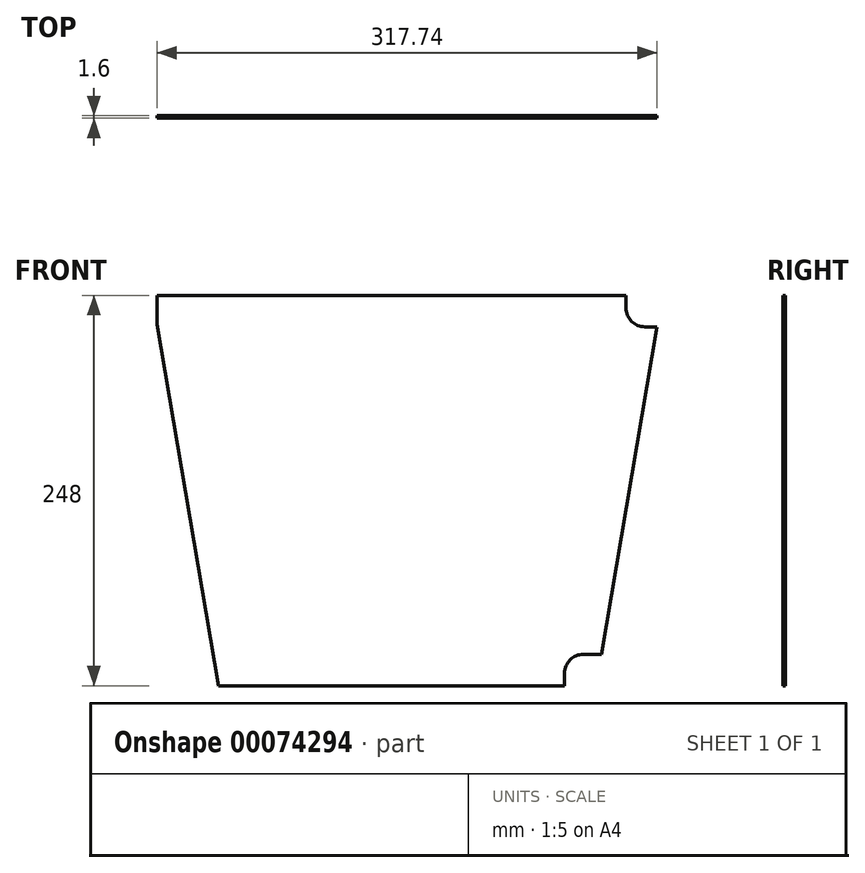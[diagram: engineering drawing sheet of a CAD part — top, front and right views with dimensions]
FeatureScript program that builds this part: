
annotation { "Feature Type Name" : "Feature", "Feature Type Description" : "" }
export const myFeature = defineFeature(function(context is Context, id is Id, definition is map)
    precondition{}
    {
        {
            var Q0;
            Q0=qCreatedBy(makeId("Front.planeOp"),FACE);
            var sketch = newSketch(context, id + "F0", { "sketchPlane" : qUnion([Q0])});
            skLineSegment(sketch, "E0.bottom", {"start": v(-165, 30.18) * mm, "end": v(165, 30.18) * mm});
            skLineSegment(sketch, "E0.left", {"start": v(-165, 30.18) * mm, "end": v(-165, 5.18) * mm});
            skLineSegment(sketch, "E0.right", {"start": v(165, 30.18) * mm, "end": v(165, 5.18) * mm});
            skLineSegment(sketch, "E1.top", {"start": v(-125, -229.82) * mm, "end": v(125, -229.82) * mm});
            skLineSegment(sketch, "E2", {"start": v(0, 0) * mm, "end": v(0, -253.16) * mm, "construction": true});
            skLineSegment(sketch, "E3", {"start": v(-165, 5.18) * mm, "end": v(-125, -229.82) * mm});
            skLineSegment(sketch, "E4", {"start": v(165, 5.18) * mm, "end": v(125, -229.82) * mm});
            skPoint(sketch, "E1.left.start.orphan", {"position": v(-125, -205.02) * mm});
            skSolve(sketch);
        }
        {
            var Q0;
            Q0=makeQuery(id+"F0.imprint","IMPRINT",FACE,{"disambiguationData":[TD([[makeQuery(id+"F0.imprint","IMPRINT",EDGE,{"derivedFrom":sQuery(id+"F0.wireOp",EDGE,"E0.bottom")}),-1.0]])]});
            extrude(context, id + "F1", {"entities" : qUnion([Q0]), "depth" : 1.6 * mm});
        }
        {
            var Q0;
            Q0=makeQuery(id+"F1.opExtrude","CAP_FACE",FACE,{"disambiguationData":[OSD([sQuery(id+"F0.wireOp",EDGE,"E0.bottom"),sQuery(id+"F0.wireOp",EDGE,"E0.left"),sQuery(id+"F0.wireOp",EDGE,"E0.right"),sQuery(id+"F0.wireOp",EDGE,"E1.top"),sQuery(id+"F0.wireOp",EDGE,"E3"),sQuery(id+"F0.wireOp",EDGE,"E4")])],"isStart":false});
            var sketch = newSketch(context, id + "F2", { "sketchPlane" : qUnion([Q0])});
            skLineSegment(sketch, "E5.0", {"start": v(-159, 24.18) * mm, "end": v(-159, 5.69) * mm});
            skLineSegment(sketch, "E5.1", {"start": v(-119.93, -223.82) * mm, "end": v(119.93, -223.82) * mm});
            skLineSegment(sketch, "E5.2", {"start": v(119.93, -223.82) * mm, "end": v(159, 5.69) * mm});
            skLineSegment(sketch, "E5.3", {"start": v(-159, 5.69) * mm, "end": v(-119.93, -223.82) * mm});
            skLineSegment(sketch, "E5.4", {"start": v(159, 5.69) * mm, "end": v(159, 24.18) * mm});
            skLineSegment(sketch, "E5.5", {"start": v(159, 24.18) * mm, "end": v(-159, 24.18) * mm});
            skLineSegment(sketch, "E6.bottom", {"start": v(-195.07, 58.7) * mm, "end": v(205.44, 58.7) * mm});
            skLineSegment(sketch, "E6.top", {"start": v(-195.07, -264.98) * mm, "end": v(205.44, -264.98) * mm});
            skLineSegment(sketch, "E6.left", {"start": v(-195.07, 58.7) * mm, "end": v(-195.07, -264.98) * mm});
            skLineSegment(sketch, "E6.right", {"start": v(205.44, 58.7) * mm, "end": v(205.44, -264.98) * mm});
            skSolve(sketch);
        }
        {
            var Q0;
            Q0 = qSketchRegion(id + "F2", true);
            extrude(context, id + "F3", {"entities" : qUnion([Q0]), "operationType" : NewBodyOperationType.REMOVE, "oppositeDirection" : true, "depth" : 25 * mm});
        }
        {
            var Q0;
            Q0=makeQuery(id+"F1.opExtrude","CAP_FACE",FACE,{"disambiguationData":[OSD([sQuery(id+"F0.wireOp",EDGE,"E0.bottom"),sQuery(id+"F0.wireOp",EDGE,"E0.left"),sQuery(id+"F0.wireOp",EDGE,"E0.right"),sQuery(id+"F0.wireOp",EDGE,"E1.top"),sQuery(id+"F0.wireOp",EDGE,"E3"),sQuery(id+"F0.wireOp",EDGE,"E4")])],"isStart":false});
            var sketch = newSketch(context, id + "F4", { "sketchPlane" : qUnion([Q0])});
            skLineSegment(sketch, "E7.bottom", {"start": v(139, 39.74) * mm, "end": v(185.07, 39.74) * mm});
            skLineSegment(sketch, "E7.top", {"start": v(139, 4.18) * mm, "end": v(185.07, 4.18) * mm});
            skLineSegment(sketch, "E7.left", {"start": v(139, 39.74) * mm, "end": v(139, 4.18) * mm});
            skLineSegment(sketch, "E7.right", {"start": v(185.07, 39.74) * mm, "end": v(185.07, 4.18) * mm});
            skSolve(sketch);
        }
        {
            var Q0;
            Q0 = qSketchRegion(id + "F4", true);
            extrude(context, id + "F5", {"entities" : qUnion([Q0]), "operationType" : NewBodyOperationType.REMOVE, "oppositeDirection" : true, "depth" : 25 * mm});
        }
        {
            var Q0;
            Q0=makeQuery(id+"F1.opExtrude","CAP_FACE",FACE,{"disambiguationData":[OSD([sQuery(id+"F0.wireOp",EDGE,"E0.bottom"),sQuery(id+"F0.wireOp",EDGE,"E0.left"),sQuery(id+"F0.wireOp",EDGE,"E0.right"),sQuery(id+"F0.wireOp",EDGE,"E1.top"),sQuery(id+"F0.wireOp",EDGE,"E3"),sQuery(id+"F0.wireOp",EDGE,"E4")])],"isStart":false});
            var sketch = newSketch(context, id + "F6", { "sketchPlane" : qUnion([Q0])});
            skLineSegment(sketch, "E8.bottom", {"start": v(99.93, -257.2) * mm, "end": v(159.27, -257.2) * mm});
            skLineSegment(sketch, "E8.top", {"start": v(99.93, -203.82) * mm, "end": v(159.27, -203.82) * mm});
            skLineSegment(sketch, "E8.left", {"start": v(99.93, -257.2) * mm, "end": v(99.93, -203.82) * mm});
            skLineSegment(sketch, "E8.right", {"start": v(159.27, -257.2) * mm, "end": v(159.27, -203.82) * mm});
            skSolve(sketch);
        }
        {
            var Q0;
            Q0 = qSketchRegion(id + "F6", true);
            extrude(context, id + "F7", {"entities" : qUnion([Q0]), "operationType" : NewBodyOperationType.REMOVE, "oppositeDirection" : true, "depth" : 25 * mm});
        }
        {
            var Q0;
            Q0=makeQuery(id+"F5.boolean.opBoolean","COPY",EDGE,{"derivedFrom":makeQuery(id+"F5.opExtrude","SWEPT_EDGE",EDGE,{"disambiguationData":[OSD([sQuery(id+"F4.wireOp",EDGE,"E7.top"),sQuery(id+"F4.wireOp",EDGE,"E7.left")])]})});
            var Q1;
            Q1=makeQuery(id+"F7.boolean.opBoolean","COPY",EDGE,{"derivedFrom":makeQuery(id+"F7.opExtrude","SWEPT_EDGE",EDGE,{"disambiguationData":[OSD([sQuery(id+"F6.wireOp",EDGE,"E8.top"),sQuery(id+"F6.wireOp",EDGE,"E8.left")])]})});
            var Q2;
            Q2=makeQuery(id+"FsGPun6Ls5V2s2E_1.1.F7.boolean.opBoolean","COPY",EDGE,{"derivedFrom":makeQuery(id+"FsGPun6Ls5V2s2E_1.1.F7.opExtrude","SWEPT_EDGE",EDGE,{"disambiguationData":[OSD([sQuery(id+"F6.wireOp",EDGE,"E8.top"),sQuery(id+"F6.wireOp",EDGE,"E8.left")])]})});
            var Q3;
            Q3=makeQuery(id+"FsGPun6Ls5V2s2E_1.1.F5.boolean.opBoolean","COPY",EDGE,{"derivedFrom":makeQuery(id+"FsGPun6Ls5V2s2E_1.1.F5.opExtrude","SWEPT_EDGE",EDGE,{"disambiguationData":[OSD([sQuery(id+"F4.wireOp",EDGE,"E7.top"),sQuery(id+"F4.wireOp",EDGE,"E7.left")])]})});
            fillet(context, id + "F8", {"entities" : qUnion([Q0, Q1, Q2, Q3]), "radius" : 12 * mm, "tangentPropagation" : true, "allowEdgeOverflow" : false});
        }
    });
